# Revit family: Data_Device-Network-Leviton-Recloseable_Storage_Ring
name_source: partatom
category: Data Devices
units: mm (PartAtom-declared; Revit-internal decimal feet)

## family parameters
Classification Number = 23.85.50.17
Cut with Voids When Loaded = No
Host = Face
Maintain Annotation Orientation = Yes
Part Type = Normal
Room Calculation Point = No
Round Connector Dimension = Use Diameter
Shared = Yes

## types (2) — shared parameters
Assembly Code = D5030600
Date Last Modified = October 05, 2023
Default Elevation = 24 "
Equipment Abbreviation = RSR
Family Version = 1.0.0
Manufacturer = Leviton
Model Disclaimer = http://www.leviton.com
Product Documentation Link = https://www.leviton.com
Ring Material = Steel- Leviton- 16 Gauge Sheet Metal
URL = http://www.leviton.com
z Offset 1 = 0.2 "
zero-valued in all types: Minimum Order Quantity, Quantity per Package

## per-type parameters (varying)
| type | Depth | Description | Height | Part Description | Width | z Center Diameter | z Internal Width | z Leviton Type | z Ring Type |
| Recloseable Storage Ring, Inside Plant | 0.06 " | Wall Mount Recloseable Storage Ring, Inside Plant, 12-inch Ring, for Fiber and Copper Cabling with Six Removable 3-inch VELCRO® Brand Loops. | 11.55 " | Wall Mount Recloseable Storage Ring, Inside Plant, 12-inch Ring, for Fiber and Copper Cabling with Six Removable 3-inch VELCRO® Brand Loops. | 11.55 " | 9.6 " | 7.75 " | 1 | Ring Inside |
| Recloseable Storage Ring, Outside Plant | 0.12 " | Wall Mount Recloseable Storage Ring, Outside Plant, 24-inch Ring, for Fiber and Copper Cabling with Six Removable 9-inch VELCRO® Brand Loops. | 24 " | Wall Mount Recloseable Storage Ring, Outside Plant, 24-inch Ring, for Fiber and Copper Cabling with Six Removable 9-inch VELCRO® Brand Loops. | 24 " | 20.5 " | 17 " | 2 | Ring Outside |

## geometry (parser evidence)
native form markers: Blend x2, Sweep x9
no freeform markers — native parametric forms only
